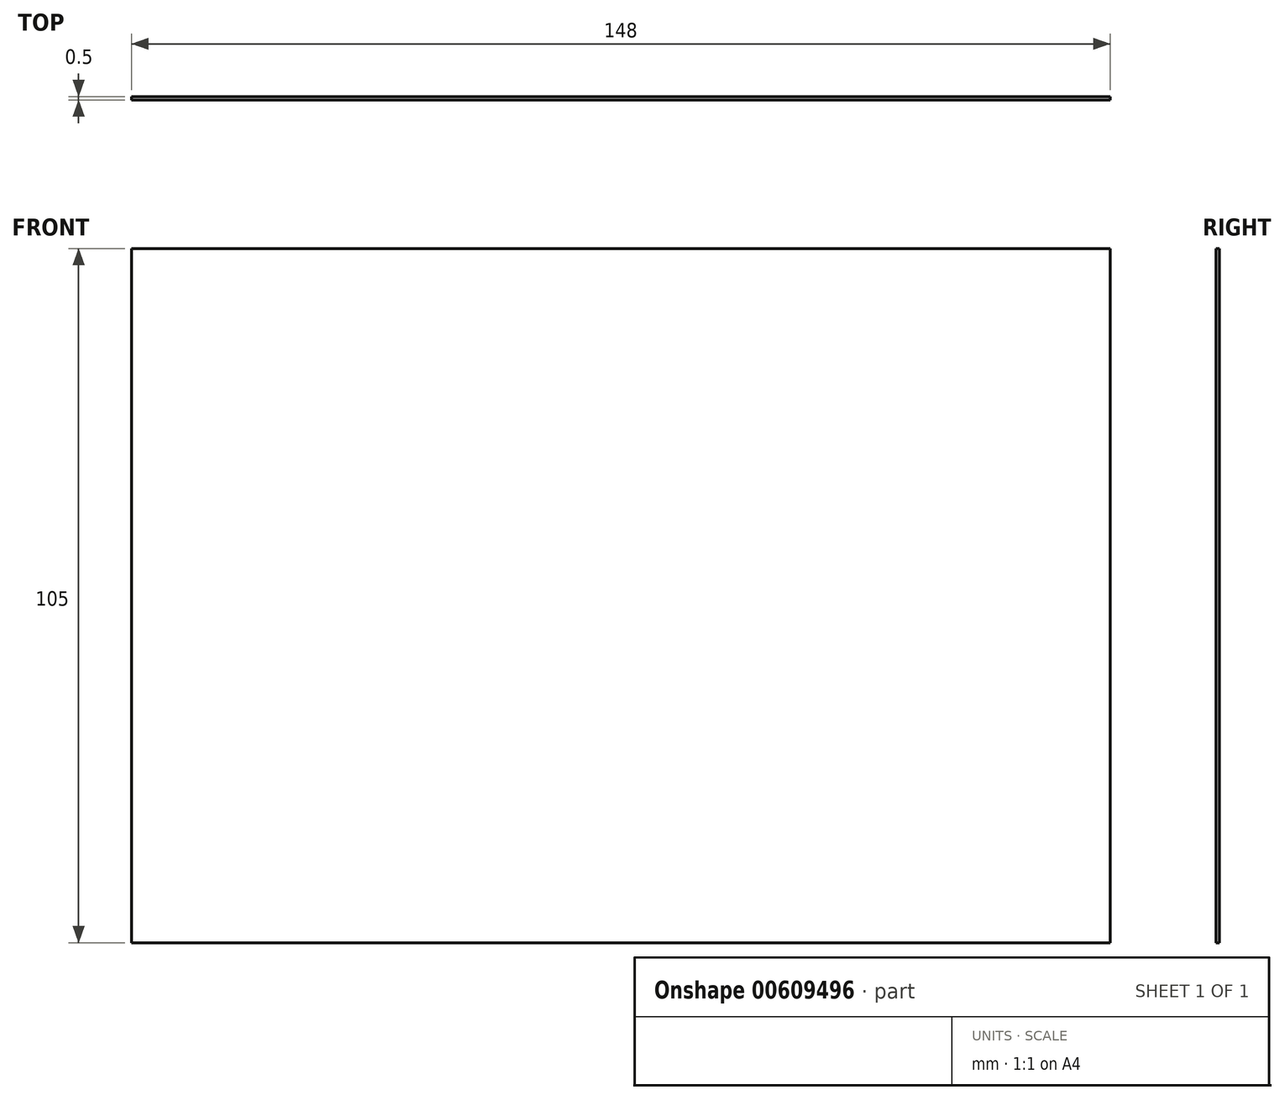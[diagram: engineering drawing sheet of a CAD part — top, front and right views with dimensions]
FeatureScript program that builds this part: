
annotation { "Feature Type Name" : "Feature", "Feature Type Description" : "" }
export const myFeature = defineFeature(function(context is Context, id is Id, definition is map)
    precondition{}
    {
        {
            var Q0;
            Q0=qCreatedBy(makeId("Front.planeOp"),FACE);
            var sketch = newSketch(context, id + "F0", { "sketchPlane" : qUnion([Q0])});
            skLineSegment(sketch, "E0.bottom", {"start": v(0, 0) * mm, "end": v(148, 0) * mm});
            skLineSegment(sketch, "E0.top", {"start": v(0, 105) * mm, "end": v(148, 105) * mm});
            skLineSegment(sketch, "E0.left", {"start": v(0, 0) * mm, "end": v(0, 105) * mm});
            skLineSegment(sketch, "E0.right", {"start": v(148, 0) * mm, "end": v(148, 105) * mm});
            skSolve(sketch);
        }
        {
            var Q0;
            Q0 = qSketchRegion(id + "F0", true);
            extrude(context, id + "F1", {"entities" : qUnion([Q0]), "depth" : 0.5 * mm, "offsetDistance" : 25 * mm});
        }
    });
